# Revit family: PRE050020-FR
name_source: partatom
category: Accessoire de canalisation
revit_build: Autodesk Revit 2017 (Build: 20160225_1515(x64)
units: mm (PartAtom-declared; Revit-internal decimal feet)

## family parameters
Basée sur le plan de construction = Non
Cote de connecteur circulaire = Utiliser le diamètre
Couper avec des vides une fois chargée = Non
Partagée = Non
Toujours verticalement = Oui
Type d'élément = Normal

## types (7) — shared parameters
Adresse = 7, RUE RACINE - 92542 MONTROUGE CEDEX FRANCE
Debit = Débit entre 4 et 6L/min à 3 bar
Diamètre Nominal = 12 mm  [stored 0.0393701 ft]
Fabricant = LES ROBINETS PRESTO S.A.
Finition = Corps et volants en laiton poli chromé
Flux = 0.1 L/s
Hauteur = 260 mm  [stored 0.853018 ft]
LC = 15 mm  [stored 0.0492126 ft]
Largeur = 50 mm  [stored 0.164042 ft]
Lien CCTP = http://www.prestodatashare.com
Lien fiche produit = http://www.prestodatashare.com
Lien notice d'utilisation = http://www.prestodatashare.com
Matériau = Laiton poli chromé
PC = 25 mm  [stored 0.082021 ft]
Perte de charge = 0.0 Pa
Pression = 3 bars
Profondeur = 194 mm  [stored 0.636483 ft]
URL = http://www.prestodatashare.com
URL Fabricant = http://www.prestodatashare.com
Variantes = 75123-75124-75125-75126-75127-75147-75163

## per-type parameters (varying)
| type | Description | Fonction | Garantie | Polantis code | Raccordement | Reference |
| 75163 Presto Sanifirst Mitigeur électronique à pile à bec fixe ou ajustable, démontable - Modul'Mix | Mitigeur hospitalier électronique pile monotrou (conception modul’mix) sans vidage pour lave-mains,livré avec commande sphérique chromée permettant le réglage de la température (commande longue disponible sur demande). Bec fixe ou orientable, lisse et démontable pour la désinfection Lg 150mm. Hauteur sous bec 100mm. Hauteur et longueur du bec adaptables sans changer toute la robinetterie. Cartouche céramique Ø 40 multifonction : butée de limitation de température  avec 7 positions de réglage, débit bloqué réglage. Cellule infra-rouge intégrée dans le corps, démontable sans dépose du robinet.  Boitier d’alimentation IP65 avec pile lithium 6V. Robinetterie montée d’origine avec un brise-jet étoile limitant le risque d’entartrage, supprimant la rétention d’eau, les impuretés et résistant aux chocs chlorés et thermiques. Corps lisse, bec et organe de manœuvre en laiton poli chromé. Flexibles avec gaine SPEX tressée inox M10X1, EP G’3/8, Lg 500mm, filtres, électrovannes avec membrane silicone M G’3/8. Fixation renforcée par une tige inox. Garantie 3 ans. Résistant aux chocs chlorés et thermiques. Programme de prévention « anti-bactérie » personnalisable (purges, fréquences, durée, etc) Marque Sanifirst type mitigeur hospitalier électronique secteur monotrou à bec fixe ou orientable lisse pour lave-mains REF : 75163 ou équivalent approuvé. | Mitigeur électronique pile

Hauteur sous bec : 100 mm

Saillie : 150 mm

Référence : 75163 | 3 ans contre tout vice de fabrication | PRE050020f-FR | Flexibles SPEX 500 mm M10 X 1 EP G'3/8 | 75163 |
| 75147 Presto Sanifirst Mitigeur électronique sur secteur à bec fixe ou ajustable, démontable - Modul'Mix | Mitigeur hospitalier électronique secteur monotrou (conception modul’mix) sans vidage pour lave-mains,livré avec commande sphérique chromée permettant le réglage de la température (commande longue disponible sur demande). Bec fixe ou orientable, lisse et démontable pour la désinfection Lg 150mm. Hauteur sous bec 100mm. Hauteur et longueur du bec adaptables sans changer toute la robinetterie. Cartouche céramique Ø 40 multifonction : butée de limitation de température  avec 7 positions de réglage, débit bloqué réglage. Cellule infra-rouge intégrée dans le corps, démontable sans dépose du robinet. Boîtier électronique secteur indépendant IP65, alimentation 230V, sortie 6V. Robinetterie montée d’origine avec un brise-jet étoile limitant le risque d’entartrage, supprimant la rétention d’eau, les impuretés et résistant aux chocs chlorés et thermiques. Corps lisse, bec et organe de manœuvre en laiton poli chromé. Flexibles avec gaine SPEX tressée inox M10X1, EP G’3/8, Lg 500mm, filtres, électrovannes avec membrane silicone M G’3/8. Fixation renforcée par une tige inox. Garantie 3 ans. Résistant aux chocs chlorés et thermiques. Programme de prévention « anti-bactérie » personnalisable (purges, fréquences, durée, etc) Marque Sanifirst type mitigeur hospitalier électronique secteur monotrou à bec fixe ou orientable lisse pour lave-mains REF : 75147 ou équivalent approuvé. | Mitigeur électronique secteur

Hauteur sous bec : 100 mm

Saillie : 150 mm

Référence : 75147 | 3 ans contre tout vice de fabrication | PRE050020e-FR | Flexibles SPEX 500 mm M10 X 1 EP G'3/8 | 75147 |
| 75127 Presto Sanifirst Mitigeur hospitalier à bec fixe ou ajustable, démontable, avec cartouche à équilibrage de pression - Modul'Mix | Mitigeur hospitalier monotrou (conception modul’mix) sans vidage pour lave-mains, avec commande longue médicale Lg 170mm qui évite le contact manuel, utilisation au coude, avant-bras ou poignet. Bec fixe ou orientable, lisse et démontable pour la désinfection Lg 150mm. Hauteur sous bec 100mm. Hauteur et longueur du bec adaptables sans changer toute la robinetterie. Cartouche céramique Ø 40 équilibrage de pression : butée de limitation de température  avec 7 positions de réglage, double débit et clapets anti retour intégrés.  Robinetterie montée d’origine avec un aérateur étoile limitant le risque d’entartrage, supprimant la rétention d’eau, les impuretés et résistant aux chocs chlorés et thermiques. Corps lisse, bec et organe de manœuvre en laiton poli chromé. Flexibles avec gaine SPEX tressée inox M10X1, EP G’3/8, Lg 500mm. Fixation renforcée par une tige inox. Garantie 10 ans. Résistant aux chocs chlorés et thermiques. Marque Sanifirst type mitigeur hospitalier équilibrage de pression monotrou à bec fixe ou orientable lisse démontable pour lave-mains REF : 75127 ou équivalent approuvé. | Mitigeur modul'mix a bec démontable

H : 100mm / S : 150mm

commande au coude

equilibrage de pression

Référence : 75127 | 10 ans contre tout vice de fabrication | PRE050020d-FR | Flexibles SPEX 350 mm M10 X 1 EP G'3/8 | 75127 |
| 75126 Presto Sanifirst Mitigeur hospitalier à bec fixe ou ajustable, démontable - Modul'Mix | Mitigeur hospitalier monotrou (conception modul’mix) sans vidage pour lave-mains, avec commande longue médicale Lg 170mm qui évite le contact manuel, utilisation au coude, avant-bras ou poignet. Bec fixe ou orientable, lisse et démontable pour la désinfection Lg 150mm. Hauteur sous bec 100mm. Hauteur et longueur du bec adaptables sans changer toute la robinetterie. Cartouche céramique Ø 40 multifonction : butée de limitation de température  avec 7 positions de réglage, double débit et réglage possible de 2l à 13,8l/min.  Robinetterie montée d’origine avec un aérateur étoile limitant le risque d’entartrage, supprimant la rétention d’eau, les impuretés et résistant aux chocs chlorés et thermiques. Corps lisse, bec et organe de manœuvre en laiton poli chromé. Flexibles avec gaine SPEX tressée inox M10X1, EP G’3/8, Lg 500mm. Fixation renforcée par une tige inox. Garantie 10 ans. Résistant aux chocs chlorés et thermiques. Marque Sanifirst type mitigeur hospitalier monotrou à bec fixe ou orientable lisse démontable pour lave-mains REF : 75126 ou équivalent approuvé. | Mitigeur modul'mix a bec démontable

H : 100mm / S : 150mm

commande au coude

Référence : 75126 | 10 ans contre tout vice de fabrication | PRE050020c-FR | Flexibles SPEX 500 mm M10 X 1 EP G'3/8 | 75126 |
| 75124 Presto Sanifirst Mitigeur hospitalier à bec fixe ou ajustable, démontable - Modul'Mix | Mitigeur hospitalier monotrou (conception modul’mix) sans vidage pour lave-mains, avec commande pleine pour nettoyage facilité. Bec fixe ou orientable, lisse et démontable pour la désinfection Lg 150mm. Hauteur sous bec 100mm. Hauteur et longueur du bec adaptables sans changer toute la robinetterie. Cartouche céramique Ø 40 multifonction : butée de limitation de température  avec 7 positions de réglage, double débit et réglage possible de 2l à 13,8l/min.  Robinetterie montée d’origine avec un aérateur étoile limitant le risque d’entartrage, supprimant la rétention d’eau, les impuretés et résistant aux chocs chlorés et thermiques. Corps lisse, bec et organe de manœuvre en laiton poli chromé. Flexibles avec gaine SPEX tressée inox M10X1, EP G’3/8, Lg 500mm. Fixation renforcée par une tige inox. Garantie 10 ans. Résistant aux chocs chlorés et thermiques. Marque Sanifirst type mitigeur hospitalier monotrou à bec fixe ou orientable lisse démontable pour lave-mains REF : 75124 ou équivalent approuvé. | Mitigeur modul'mix a bec démontable

H : 100mm / S : 150mm

Référence : 75124 | 10 ans contre tout vice de fabrication | PRE050020a-FR | Flexibles SPEX 500 mm M10 X 1 EP G'3/8 | 75124 |
| 75123 Presto Sanifirst Mitigeur hospitalier monotrou à bec fixe ou ajustable, décliptable - Modul'Mix | Mitigeur hospitalier monotrou (conception modul’mix) sans vidage pour lave-mains, avec commande longue médicale Lg 170mm qui évite le contact manuel, utilisation au coude, avant-bras ou poignet. Bec fixe ou orientable, lisse et décliptable avec obturation pour la désinfection Lg 150mm. Hauteur sous bec 100mm. Hauteur et longueur du bec adaptables sans changer toute la robinetterie. Cartouche céramique Ø 40 multifonction : butée de limitation de température  avec 7 positions de réglage, double débit et réglage possible de 2l à 13,8l/min.  Robinetterie montée d’origine avec un aérateur étoile limitant le risque d’entartrage, supprimant la rétention d’eau, les impuretés et résistant aux chocs chlorés et thermiques. Corps lisse, bec et organe de manœuvre en laiton poli chromé. Flexibles avec gaine SPEX tressée inox M10X1, EP G’3/8, Lg 500mm. Fixation renforcée par une tige inox. Garantie 10 ans. Résistant aux chocs chlorés et thermiques. Marque Sanifirst type mitigeur hospitalier monotrou à bec fixe ou orientable lisse décliptable pour lave-mains REF : 75123 ou équivalent approuvé. | Mitigeur modul'mix a bec decliptable

H : 100mm / S : 150mm

commande au coude

Référence : 75123 | 10 ans contre tout vice de fabrication | PRE050020-FR | Flexibles SPEX 500 mm M10 X 1 EP G'3/8 | 75123 |
| 75125 Presto Sanifirst Mitigeur hospitalier à bec fixe ou ajustable, démontable, avec cartouche à équilibrage de pression - Modul'Mix | Mitigeur hospitalier monotrou (conception modul’mix) sans vidage pour lave-mains, avec commande pleine pour nettoyage facilité. Bec fixe ou orientable, lisse et démontable pour la désinfection Lg 150mm. Hauteur sous bec 100mm. Hauteur et longueur du bec adaptables sans changer toute la robinetterie. Cartouche céramique Ø 40 équilibrage de pression : butée de limitation de température  avec 7 positions de réglage, double débit et clapets anti retour intégrés.  Robinetterie montée d’origine avec un aérateur étoile limitant le risque d’entartrage, supprimant la rétention d’eau, les impuretés et résistant aux chocs chlorés et thermiques. Corps lisse, bec et organe de manœuvre en laiton poli chromé. Flexibles avec gaine SPEX tressée inox M10X1, EP G’3/8, Lg 500mm. Fixation renforcée par une tige inox. Garantie 10 ans. Résistant aux chocs chlorés et thermiques. Marque Sanifirst type mitigeur hospitalier équilibrage de pression monotrou à bec fixe ou orientable lisse démontable pour lave-mains REF : 75125 ou équivalent approuvé. | Mitigeur modul'mix a bec démontable

H : 100mm / S : 150mm

équilibrage de pression

Référence : 75125 | 10 ans contre tout vice de fabrication | PRE050020b-FR | Flexibles SPEX 500 mm M10 X 1 EP G'3/8 | 75125 |

note: column(s) folded — value = type name in every type: Modèle

note: [stored X ft] marks values corroborated as IEEE doubles in the binary element streams (Revit-internal decimal feet)
